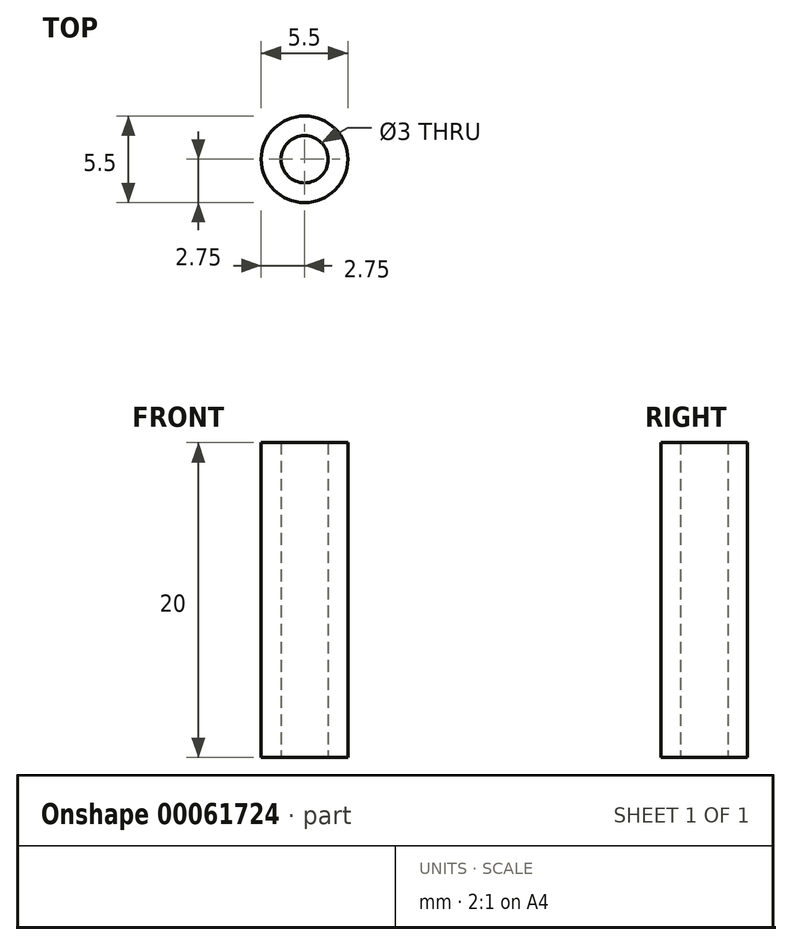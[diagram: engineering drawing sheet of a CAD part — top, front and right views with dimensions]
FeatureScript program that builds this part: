
annotation { "Feature Type Name" : "Feature", "Feature Type Description" : "" }
export const myFeature = defineFeature(function(context is Context, id is Id, definition is map)
    precondition{}
    {
        {
            var Q0;
            Q0=qCreatedBy(makeId("Top.planeOp"),FACE);
            var sketch = newSketch(context, id + "F0", { "sketchPlane" : qUnion([Q0])});
            skCircle(sketch, "E0", {"center": v(0, 0) * mm, "radius": 1.5 * mm});
            skCircle(sketch, "E1", {"center": v(0, 0) * mm, "radius": 2.75 * mm});
            skSolve(sketch);
        }
        {
            var Q0;
            Q0 = qSketchRegion(id + "F0", true);
            extrude(context, id + "F1", {"entities" : qUnion([Q0]), "depth" : 20 * mm});
        }
    });
